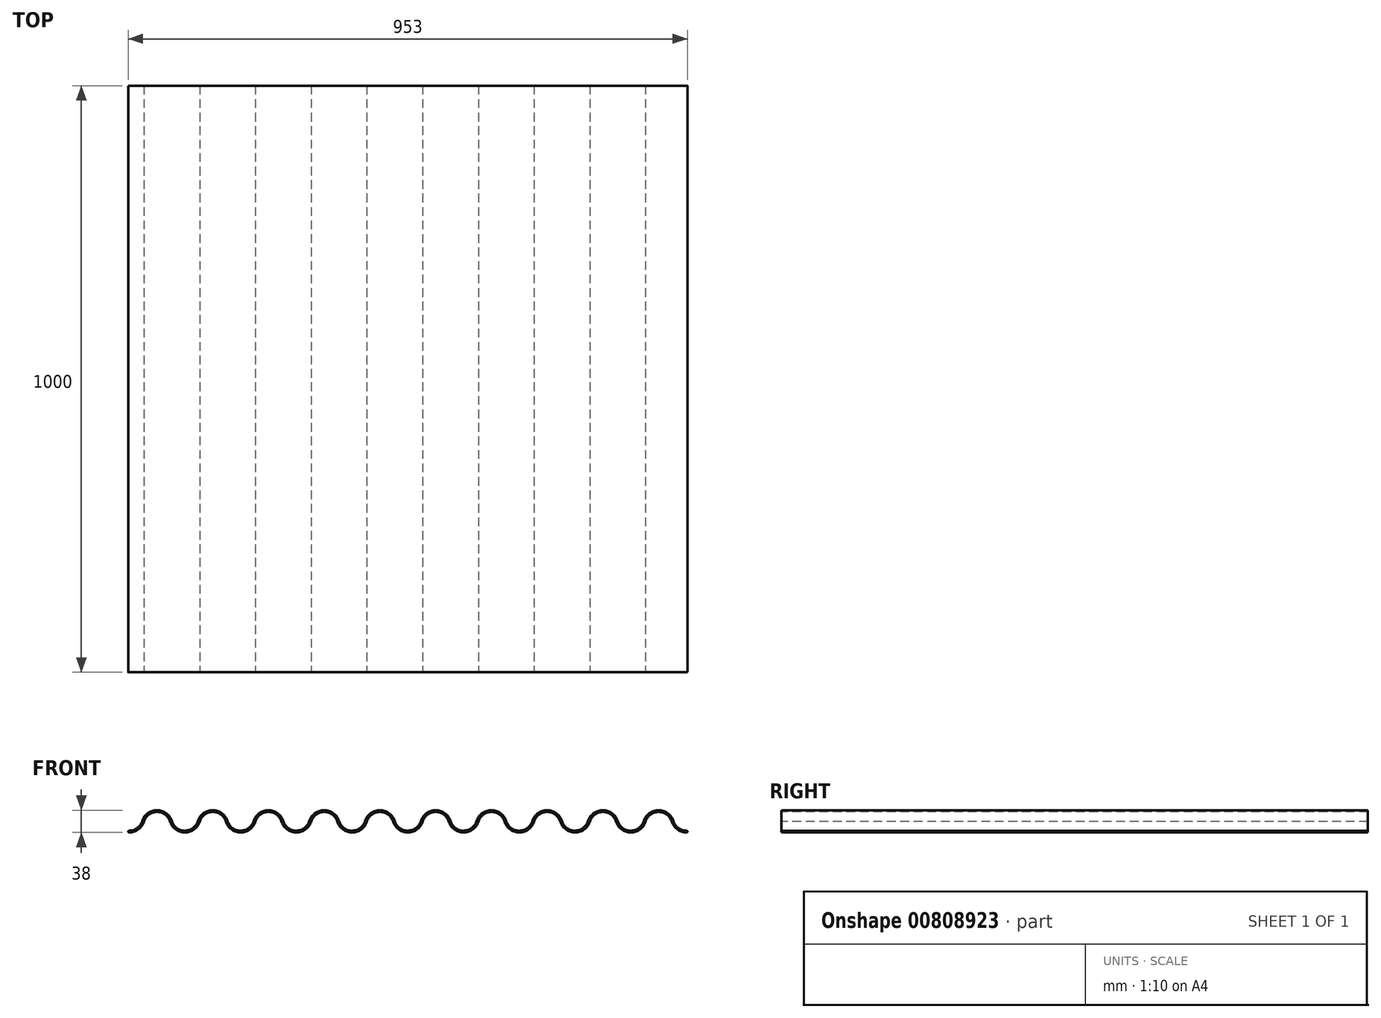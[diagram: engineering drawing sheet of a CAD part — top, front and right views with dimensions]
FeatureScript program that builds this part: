
annotation { "Feature Type Name" : "Feature", "Feature Type Description" : "" }
export const myFeature = defineFeature(function(context is Context, id is Id, definition is map)
    precondition{}
    {
        {
            var Q0;
            Q0=qCreatedBy(makeId("Front.planeOp"),FACE);
            var sketch = newSketch(context, id + "F0", { "sketchPlane" : qUnion([Q0])});
            skPoint(sketch, "E0.middle", {"position": v(0, 0) * mm});
            skArc(sketch, "E1", {"start": v(-47.5, -17.5) * mm, "mid": v(-32.61, -12.55) * mm, "end": v(-23.65, 0.32) * mm});
            skArc(sketch, "E2", {"start": v(0, 17.5) * mm, "mid": v(-14.62, 12.75) * mm, "end": v(-23.65, 0.32) * mm});
            skArc(sketch, "E3", {"start": v(23.75, 0) * mm, "mid": v(14.76, 12.66) * mm, "end": v(0, 17.5) * mm});
            skArc(sketch, "E4", {"start": v(23.75, 0) * mm, "mid": v(32.75, -12.65) * mm, "end": v(47.5, -17.5) * mm});
            skArc(sketch, "E5.0.startCap", {"start": v(-47.5, -19) * mm, "mid": v(-49, -17.5) * mm, "end": v(-47.5, -16) * mm});
            skArc(sketch, "E5.0.endCap", {"start": v(-25.1, 0.75) * mm, "mid": v(-23.23, 1.76) * mm, "end": v(-22.21, -0.1) * mm});
            skArc(sketch, "E5.0.left", {"start": v(-47.5, -16) * mm, "mid": v(-33.51, -11.35) * mm, "end": v(-25.1, 0.75) * mm});
            skArc(sketch, "E5.0.right", {"start": v(-47.5, -19) * mm, "mid": v(-31.72, -13.75) * mm, "end": v(-22.21, -0.1) * mm});
            skArc(sketch, "E5.1.startCap", {"start": v(0, 19) * mm, "mid": v(1.5, 17.5) * mm, "end": v(0, 16) * mm});
            skArc(sketch, "E5.1.endCap", {"start": v(-22.23, -0.14) * mm, "mid": v(-24.12, -1.1) * mm, "end": v(-25.08, 0.79) * mm});
            skArc(sketch, "E5.1.left", {"start": v(0, 16) * mm, "mid": v(-13.73, 11.54) * mm, "end": v(-22.23, -0.14) * mm});
            skArc(sketch, "E5.1.right", {"start": v(0, 19) * mm, "mid": v(-15.5, 13.97) * mm, "end": v(-25.08, 0.79) * mm});
            skArc(sketch, "E5.2.startCap", {"start": v(25.18, 0.44) * mm, "mid": v(24.2, -1.43) * mm, "end": v(22.32, -0.44) * mm});
            skArc(sketch, "E5.2.endCap", {"start": v(0, 16) * mm, "mid": v(-1.5, 17.5) * mm, "end": v(0, 19) * mm});
            skArc(sketch, "E5.2.left", {"start": v(22.32, -0.44) * mm, "mid": v(13.87, 11.46) * mm, "end": v(0, 16) * mm});
            skArc(sketch, "E5.2.right", {"start": v(25.18, 0.44) * mm, "mid": v(15.65, 13.87) * mm, "end": v(0, 19) * mm});
            skArc(sketch, "E5.3.startCap", {"start": v(22.32, -0.44) * mm, "mid": v(23.3, 1.43) * mm, "end": v(25.18, 0.44) * mm});
            skArc(sketch, "E5.3.endCap", {"start": v(47.5, -16) * mm, "mid": v(49, -17.5) * mm, "end": v(47.5, -19) * mm});
            skArc(sketch, "E5.3.left", {"start": v(25.18, 0.44) * mm, "mid": v(33.64, -11.44) * mm, "end": v(47.5, -16) * mm});
            skArc(sketch, "E5.3.right", {"start": v(22.32, -0.44) * mm, "mid": v(31.86, -13.86) * mm, "end": v(47.5, -19) * mm});
            skArc(sketch, "E6.1.0.0", {"start": v(47.5, -19) * mm, "mid": v(63.28, -13.75) * mm, "end": v(72.79, -0.1) * mm});
            skArc(sketch, "E6.1.0.1", {"start": v(95, 19) * mm, "mid": v(79.5, 13.97) * mm, "end": v(69.92, 0.79) * mm});
            skArc(sketch, "E6.1.0.2", {"start": v(118.75, 0) * mm, "mid": v(109.76, 12.66) * mm, "end": v(95, 17.5) * mm});
            skArc(sketch, "E6.1.0.3", {"start": v(72.77, -0.14) * mm, "mid": v(70.88, -1.1) * mm, "end": v(69.92, 0.79) * mm});
            skArc(sketch, "E6.1.0.4", {"start": v(47.5, -17.5) * mm, "mid": v(62.39, -12.55) * mm, "end": v(71.35, 0.32) * mm});
            skArc(sketch, "E6.1.0.5", {"start": v(118.75, 0) * mm, "mid": v(127.75, -12.65) * mm, "end": v(142.5, -17.5) * mm});
            skArc(sketch, "E6.1.0.6", {"start": v(95, 17.5) * mm, "mid": v(80.38, 12.75) * mm, "end": v(71.35, 0.32) * mm});
            skPoint(sketch, "E6.1.0.7", {"position": v(95, 0) * mm});
            skArc(sketch, "E6.1.0.8", {"start": v(95, 16) * mm, "mid": v(81.27, 11.54) * mm, "end": v(72.77, -0.14) * mm});
            skArc(sketch, "E6.1.0.9", {"start": v(117.32, -0.44) * mm, "mid": v(108.87, 11.46) * mm, "end": v(95, 16) * mm});
            skArc(sketch, "E6.1.0.10", {"start": v(120.18, 0.44) * mm, "mid": v(128.64, -11.44) * mm, "end": v(142.5, -16) * mm});
            skArc(sketch, "E6.1.0.11", {"start": v(95, 19) * mm, "mid": v(96.5, 17.5) * mm, "end": v(95, 16) * mm});
            skArc(sketch, "E6.1.0.12", {"start": v(47.5, -16) * mm, "mid": v(61.49, -11.35) * mm, "end": v(69.9, 0.75) * mm});
            skArc(sketch, "E6.1.0.13", {"start": v(117.32, -0.44) * mm, "mid": v(126.86, -13.86) * mm, "end": v(142.5, -19) * mm});
            skArc(sketch, "E6.1.0.14", {"start": v(120.18, 0.44) * mm, "mid": v(119.2, -1.43) * mm, "end": v(117.32, -0.44) * mm});
            skArc(sketch, "E6.1.0.15", {"start": v(47.5, -19) * mm, "mid": v(46, -17.5) * mm, "end": v(47.5, -16) * mm});
            skArc(sketch, "E6.1.0.16", {"start": v(69.9, 0.75) * mm, "mid": v(71.77, 1.76) * mm, "end": v(72.79, -0.1) * mm});
            skArc(sketch, "E6.1.0.17", {"start": v(142.5, -16) * mm, "mid": v(144, -17.5) * mm, "end": v(142.5, -19) * mm});
            skArc(sketch, "E6.1.0.18", {"start": v(120.18, 0.44) * mm, "mid": v(110.65, 13.87) * mm, "end": v(95, 19) * mm});
            skArc(sketch, "E6.1.0.19", {"start": v(117.32, -0.44) * mm, "mid": v(118.3, 1.43) * mm, "end": v(120.18, 0.44) * mm});
            skArc(sketch, "E6.1.0.20", {"start": v(95, 16) * mm, "mid": v(93.5, 17.5) * mm, "end": v(95, 19) * mm});
            skArc(sketch, "E6.2.0.0", {"start": v(142.5, -19) * mm, "mid": v(158.28, -13.75) * mm, "end": v(167.79, -0.1) * mm});
            skArc(sketch, "E6.2.0.1", {"start": v(190, 19) * mm, "mid": v(174.5, 13.97) * mm, "end": v(164.92, 0.79) * mm});
            skArc(sketch, "E6.2.0.2", {"start": v(213.75, 0) * mm, "mid": v(204.76, 12.66) * mm, "end": v(190, 17.5) * mm});
            skArc(sketch, "E6.2.0.3", {"start": v(167.77, -0.14) * mm, "mid": v(165.88, -1.1) * mm, "end": v(164.92, 0.79) * mm});
            skArc(sketch, "E6.2.0.4", {"start": v(142.5, -17.5) * mm, "mid": v(157.39, -12.55) * mm, "end": v(166.35, 0.32) * mm});
            skArc(sketch, "E6.2.0.5", {"start": v(213.75, 0) * mm, "mid": v(222.75, -12.65) * mm, "end": v(237.5, -17.5) * mm});
            skArc(sketch, "E6.2.0.6", {"start": v(190, 17.5) * mm, "mid": v(175.38, 12.75) * mm, "end": v(166.35, 0.32) * mm});
            skPoint(sketch, "E6.2.0.7", {"position": v(190, 0) * mm});
            skArc(sketch, "E6.2.0.8", {"start": v(190, 16) * mm, "mid": v(176.27, 11.54) * mm, "end": v(167.77, -0.14) * mm});
            skArc(sketch, "E6.2.0.9", {"start": v(212.32, -0.44) * mm, "mid": v(203.87, 11.46) * mm, "end": v(190, 16) * mm});
            skArc(sketch, "E6.2.0.10", {"start": v(215.18, 0.44) * mm, "mid": v(223.64, -11.44) * mm, "end": v(237.5, -16) * mm});
            skArc(sketch, "E6.2.0.11", {"start": v(190, 19) * mm, "mid": v(191.5, 17.5) * mm, "end": v(190, 16) * mm});
            skArc(sketch, "E6.2.0.12", {"start": v(142.5, -16) * mm, "mid": v(156.49, -11.35) * mm, "end": v(164.9, 0.75) * mm});
            skArc(sketch, "E6.2.0.13", {"start": v(212.32, -0.44) * mm, "mid": v(221.86, -13.86) * mm, "end": v(237.5, -19) * mm});
            skArc(sketch, "E6.2.0.14", {"start": v(215.18, 0.44) * mm, "mid": v(214.2, -1.43) * mm, "end": v(212.32, -0.44) * mm});
            skArc(sketch, "E6.2.0.15", {"start": v(142.5, -19) * mm, "mid": v(141, -17.5) * mm, "end": v(142.5, -16) * mm});
            skArc(sketch, "E6.2.0.16", {"start": v(164.9, 0.75) * mm, "mid": v(166.77, 1.76) * mm, "end": v(167.79, -0.1) * mm});
            skArc(sketch, "E6.2.0.17", {"start": v(237.5, -16) * mm, "mid": v(239, -17.5) * mm, "end": v(237.5, -19) * mm});
            skArc(sketch, "E6.2.0.18", {"start": v(215.18, 0.44) * mm, "mid": v(205.65, 13.87) * mm, "end": v(190, 19) * mm});
            skArc(sketch, "E6.2.0.19", {"start": v(212.32, -0.44) * mm, "mid": v(213.3, 1.43) * mm, "end": v(215.18, 0.44) * mm});
            skArc(sketch, "E6.2.0.20", {"start": v(190, 16) * mm, "mid": v(188.5, 17.5) * mm, "end": v(190, 19) * mm});
            skArc(sketch, "E6.3.0.0", {"start": v(237.5, -19) * mm, "mid": v(253.28, -13.75) * mm, "end": v(262.79, -0.1) * mm});
            skArc(sketch, "E6.3.0.1", {"start": v(285, 19) * mm, "mid": v(269.5, 13.97) * mm, "end": v(259.92, 0.79) * mm});
            skArc(sketch, "E6.3.0.2", {"start": v(308.75, 0) * mm, "mid": v(299.76, 12.66) * mm, "end": v(285, 17.5) * mm});
            skArc(sketch, "E6.3.0.3", {"start": v(262.77, -0.14) * mm, "mid": v(260.88, -1.1) * mm, "end": v(259.92, 0.79) * mm});
            skArc(sketch, "E6.3.0.4", {"start": v(237.5, -17.5) * mm, "mid": v(252.39, -12.55) * mm, "end": v(261.35, 0.32) * mm});
            skArc(sketch, "E6.3.0.5", {"start": v(308.75, 0) * mm, "mid": v(317.75, -12.65) * mm, "end": v(332.5, -17.5) * mm});
            skArc(sketch, "E6.3.0.6", {"start": v(285, 17.5) * mm, "mid": v(270.38, 12.75) * mm, "end": v(261.35, 0.32) * mm});
            skPoint(sketch, "E6.3.0.7", {"position": v(285, 0) * mm});
            skArc(sketch, "E6.3.0.8", {"start": v(285, 16) * mm, "mid": v(271.27, 11.54) * mm, "end": v(262.77, -0.14) * mm});
            skArc(sketch, "E6.3.0.9", {"start": v(307.32, -0.44) * mm, "mid": v(298.87, 11.46) * mm, "end": v(285, 16) * mm});
            skArc(sketch, "E6.3.0.10", {"start": v(310.18, 0.44) * mm, "mid": v(318.64, -11.44) * mm, "end": v(332.5, -16) * mm});
            skArc(sketch, "E6.3.0.11", {"start": v(285, 19) * mm, "mid": v(286.5, 17.5) * mm, "end": v(285, 16) * mm});
            skArc(sketch, "E6.3.0.12", {"start": v(237.5, -16) * mm, "mid": v(251.49, -11.35) * mm, "end": v(259.9, 0.75) * mm});
            skArc(sketch, "E6.3.0.13", {"start": v(307.32, -0.44) * mm, "mid": v(316.86, -13.86) * mm, "end": v(332.5, -19) * mm});
            skArc(sketch, "E6.3.0.14", {"start": v(310.18, 0.44) * mm, "mid": v(309.2, -1.43) * mm, "end": v(307.32, -0.44) * mm});
            skArc(sketch, "E6.3.0.15", {"start": v(237.5, -19) * mm, "mid": v(236, -17.5) * mm, "end": v(237.5, -16) * mm});
            skArc(sketch, "E6.3.0.16", {"start": v(259.9, 0.75) * mm, "mid": v(261.77, 1.76) * mm, "end": v(262.79, -0.1) * mm});
            skArc(sketch, "E6.3.0.17", {"start": v(332.5, -16) * mm, "mid": v(334, -17.5) * mm, "end": v(332.5, -19) * mm});
            skArc(sketch, "E6.3.0.18", {"start": v(310.18, 0.44) * mm, "mid": v(300.65, 13.87) * mm, "end": v(285, 19) * mm});
            skArc(sketch, "E6.3.0.19", {"start": v(307.32, -0.44) * mm, "mid": v(308.3, 1.43) * mm, "end": v(310.18, 0.44) * mm});
            skArc(sketch, "E6.3.0.20", {"start": v(285, 16) * mm, "mid": v(283.5, 17.5) * mm, "end": v(285, 19) * mm});
            skArc(sketch, "E6.4.0.0", {"start": v(332.5, -19) * mm, "mid": v(348.28, -13.75) * mm, "end": v(357.79, -0.1) * mm});
            skArc(sketch, "E6.4.0.1", {"start": v(380, 19) * mm, "mid": v(364.5, 13.97) * mm, "end": v(354.92, 0.79) * mm});
            skArc(sketch, "E6.4.0.2", {"start": v(403.75, 0) * mm, "mid": v(394.76, 12.66) * mm, "end": v(380, 17.5) * mm});
            skArc(sketch, "E6.4.0.3", {"start": v(357.77, -0.14) * mm, "mid": v(355.88, -1.1) * mm, "end": v(354.92, 0.79) * mm});
            skArc(sketch, "E6.4.0.4", {"start": v(332.5, -17.5) * mm, "mid": v(347.39, -12.55) * mm, "end": v(356.35, 0.32) * mm});
            skArc(sketch, "E6.4.0.5", {"start": v(403.75, 0) * mm, "mid": v(412.75, -12.65) * mm, "end": v(427.5, -17.5) * mm});
            skArc(sketch, "E6.4.0.6", {"start": v(380, 17.5) * mm, "mid": v(365.38, 12.75) * mm, "end": v(356.35, 0.32) * mm});
            skPoint(sketch, "E6.4.0.7", {"position": v(380, 0) * mm});
            skArc(sketch, "E6.4.0.8", {"start": v(380, 16) * mm, "mid": v(366.27, 11.54) * mm, "end": v(357.77, -0.14) * mm});
            skArc(sketch, "E6.4.0.9", {"start": v(402.32, -0.44) * mm, "mid": v(393.87, 11.46) * mm, "end": v(380, 16) * mm});
            skArc(sketch, "E6.4.0.10", {"start": v(405.18, 0.44) * mm, "mid": v(413.64, -11.44) * mm, "end": v(427.5, -16) * mm});
            skArc(sketch, "E6.4.0.11", {"start": v(380, 19) * mm, "mid": v(381.5, 17.5) * mm, "end": v(380, 16) * mm});
            skArc(sketch, "E6.4.0.12", {"start": v(332.5, -16) * mm, "mid": v(346.49, -11.35) * mm, "end": v(354.9, 0.75) * mm});
            skArc(sketch, "E6.4.0.13", {"start": v(402.32, -0.44) * mm, "mid": v(411.86, -13.86) * mm, "end": v(427.5, -19) * mm});
            skArc(sketch, "E6.4.0.14", {"start": v(405.18, 0.44) * mm, "mid": v(404.2, -1.43) * mm, "end": v(402.32, -0.44) * mm});
            skArc(sketch, "E6.4.0.15", {"start": v(332.5, -19) * mm, "mid": v(331, -17.5) * mm, "end": v(332.5, -16) * mm});
            skArc(sketch, "E6.4.0.16", {"start": v(354.9, 0.75) * mm, "mid": v(356.77, 1.76) * mm, "end": v(357.79, -0.1) * mm});
            skArc(sketch, "E6.4.0.17", {"start": v(427.5, -16) * mm, "mid": v(429, -17.5) * mm, "end": v(427.5, -19) * mm});
            skArc(sketch, "E6.4.0.18", {"start": v(405.18, 0.44) * mm, "mid": v(395.65, 13.87) * mm, "end": v(380, 19) * mm});
            skArc(sketch, "E6.4.0.19", {"start": v(402.32, -0.44) * mm, "mid": v(403.3, 1.43) * mm, "end": v(405.18, 0.44) * mm});
            skArc(sketch, "E6.4.0.20", {"start": v(380, 16) * mm, "mid": v(378.5, 17.5) * mm, "end": v(380, 19) * mm});
            skArc(sketch, "E6.5.0.0", {"start": v(427.5, -19) * mm, "mid": v(443.28, -13.75) * mm, "end": v(452.79, -0.1) * mm});
            skArc(sketch, "E6.5.0.1", {"start": v(475, 19) * mm, "mid": v(459.5, 13.97) * mm, "end": v(449.92, 0.79) * mm});
            skArc(sketch, "E6.5.0.2", {"start": v(498.75, 0) * mm, "mid": v(489.76, 12.66) * mm, "end": v(475, 17.5) * mm});
            skArc(sketch, "E6.5.0.3", {"start": v(452.77, -0.14) * mm, "mid": v(450.88, -1.1) * mm, "end": v(449.92, 0.79) * mm});
            skArc(sketch, "E6.5.0.4", {"start": v(427.5, -17.5) * mm, "mid": v(442.39, -12.55) * mm, "end": v(451.35, 0.32) * mm});
            skArc(sketch, "E6.5.0.5", {"start": v(498.75, 0) * mm, "mid": v(507.75, -12.65) * mm, "end": v(522.5, -17.5) * mm});
            skArc(sketch, "E6.5.0.6", {"start": v(475, 17.5) * mm, "mid": v(460.38, 12.75) * mm, "end": v(451.35, 0.32) * mm});
            skPoint(sketch, "E6.5.0.7", {"position": v(475, 0) * mm});
            skArc(sketch, "E6.5.0.8", {"start": v(475, 16) * mm, "mid": v(461.27, 11.54) * mm, "end": v(452.77, -0.14) * mm});
            skArc(sketch, "E6.5.0.9", {"start": v(497.32, -0.44) * mm, "mid": v(488.87, 11.46) * mm, "end": v(475, 16) * mm});
            skArc(sketch, "E6.5.0.10", {"start": v(500.18, 0.44) * mm, "mid": v(508.64, -11.44) * mm, "end": v(522.5, -16) * mm});
            skArc(sketch, "E6.5.0.11", {"start": v(475, 19) * mm, "mid": v(476.5, 17.5) * mm, "end": v(475, 16) * mm});
            skArc(sketch, "E6.5.0.12", {"start": v(427.5, -16) * mm, "mid": v(441.49, -11.35) * mm, "end": v(449.9, 0.75) * mm});
            skArc(sketch, "E6.5.0.13", {"start": v(497.32, -0.44) * mm, "mid": v(506.86, -13.86) * mm, "end": v(522.5, -19) * mm});
            skArc(sketch, "E6.5.0.14", {"start": v(500.18, 0.44) * mm, "mid": v(499.2, -1.43) * mm, "end": v(497.32, -0.44) * mm});
            skArc(sketch, "E6.5.0.15", {"start": v(427.5, -19) * mm, "mid": v(426, -17.5) * mm, "end": v(427.5, -16) * mm});
            skArc(sketch, "E6.5.0.16", {"start": v(449.9, 0.75) * mm, "mid": v(451.77, 1.76) * mm, "end": v(452.79, -0.1) * mm});
            skArc(sketch, "E6.5.0.17", {"start": v(522.5, -16) * mm, "mid": v(524, -17.5) * mm, "end": v(522.5, -19) * mm});
            skArc(sketch, "E6.5.0.18", {"start": v(500.18, 0.44) * mm, "mid": v(490.65, 13.87) * mm, "end": v(475, 19) * mm});
            skArc(sketch, "E6.5.0.19", {"start": v(497.32, -0.44) * mm, "mid": v(498.3, 1.43) * mm, "end": v(500.18, 0.44) * mm});
            skArc(sketch, "E6.5.0.20", {"start": v(475, 16) * mm, "mid": v(473.5, 17.5) * mm, "end": v(475, 19) * mm});
            skArc(sketch, "E6.6.0.0", {"start": v(522.5, -19) * mm, "mid": v(538.28, -13.75) * mm, "end": v(547.79, -0.1) * mm});
            skArc(sketch, "E6.6.0.1", {"start": v(570, 19) * mm, "mid": v(554.5, 13.97) * mm, "end": v(544.92, 0.79) * mm});
            skArc(sketch, "E6.6.0.2", {"start": v(593.75, 0) * mm, "mid": v(584.76, 12.66) * mm, "end": v(570, 17.5) * mm});
            skArc(sketch, "E6.6.0.3", {"start": v(547.77, -0.14) * mm, "mid": v(545.88, -1.1) * mm, "end": v(544.92, 0.79) * mm});
            skArc(sketch, "E6.6.0.4", {"start": v(522.5, -17.5) * mm, "mid": v(537.39, -12.55) * mm, "end": v(546.35, 0.32) * mm});
            skArc(sketch, "E6.6.0.5", {"start": v(593.75, 0) * mm, "mid": v(602.75, -12.65) * mm, "end": v(617.5, -17.5) * mm});
            skArc(sketch, "E6.6.0.6", {"start": v(570, 17.5) * mm, "mid": v(555.38, 12.75) * mm, "end": v(546.35, 0.32) * mm});
            skPoint(sketch, "E6.6.0.7", {"position": v(570, 0) * mm});
            skArc(sketch, "E6.6.0.8", {"start": v(570, 16) * mm, "mid": v(556.27, 11.54) * mm, "end": v(547.77, -0.14) * mm});
            skArc(sketch, "E6.6.0.9", {"start": v(592.32, -0.44) * mm, "mid": v(583.87, 11.46) * mm, "end": v(570, 16) * mm});
            skArc(sketch, "E6.6.0.10", {"start": v(595.18, 0.44) * mm, "mid": v(603.64, -11.44) * mm, "end": v(617.5, -16) * mm});
            skArc(sketch, "E6.6.0.11", {"start": v(570, 19) * mm, "mid": v(571.5, 17.5) * mm, "end": v(570, 16) * mm});
            skArc(sketch, "E6.6.0.12", {"start": v(522.5, -16) * mm, "mid": v(536.49, -11.35) * mm, "end": v(544.9, 0.75) * mm});
            skArc(sketch, "E6.6.0.13", {"start": v(592.32, -0.44) * mm, "mid": v(601.86, -13.86) * mm, "end": v(617.5, -19) * mm});
            skArc(sketch, "E6.6.0.14", {"start": v(595.18, 0.44) * mm, "mid": v(594.2, -1.43) * mm, "end": v(592.32, -0.44) * mm});
            skArc(sketch, "E6.6.0.15", {"start": v(522.5, -19) * mm, "mid": v(521, -17.5) * mm, "end": v(522.5, -16) * mm});
            skArc(sketch, "E6.6.0.16", {"start": v(544.9, 0.75) * mm, "mid": v(546.77, 1.76) * mm, "end": v(547.79, -0.1) * mm});
            skArc(sketch, "E6.6.0.17", {"start": v(617.5, -16) * mm, "mid": v(619, -17.5) * mm, "end": v(617.5, -19) * mm});
            skArc(sketch, "E6.6.0.18", {"start": v(595.18, 0.44) * mm, "mid": v(585.65, 13.87) * mm, "end": v(570, 19) * mm});
            skArc(sketch, "E6.6.0.19", {"start": v(592.32, -0.44) * mm, "mid": v(593.3, 1.43) * mm, "end": v(595.18, 0.44) * mm});
            skArc(sketch, "E6.6.0.20", {"start": v(570, 16) * mm, "mid": v(568.5, 17.5) * mm, "end": v(570, 19) * mm});
            skArc(sketch, "E6.7.0.0", {"start": v(617.5, -19) * mm, "mid": v(633.28, -13.75) * mm, "end": v(642.79, -0.1) * mm});
            skArc(sketch, "E6.7.0.1", {"start": v(665, 19) * mm, "mid": v(649.5, 13.97) * mm, "end": v(639.92, 0.79) * mm});
            skArc(sketch, "E6.7.0.2", {"start": v(688.75, 0) * mm, "mid": v(679.76, 12.66) * mm, "end": v(665, 17.5) * mm});
            skArc(sketch, "E6.7.0.3", {"start": v(642.77, -0.14) * mm, "mid": v(640.88, -1.1) * mm, "end": v(639.92, 0.79) * mm});
            skArc(sketch, "E6.7.0.4", {"start": v(617.5, -17.5) * mm, "mid": v(632.39, -12.55) * mm, "end": v(641.35, 0.32) * mm});
            skArc(sketch, "E6.7.0.5", {"start": v(688.75, 0) * mm, "mid": v(697.75, -12.65) * mm, "end": v(712.5, -17.5) * mm});
            skArc(sketch, "E6.7.0.6", {"start": v(665, 17.5) * mm, "mid": v(650.38, 12.75) * mm, "end": v(641.35, 0.32) * mm});
            skPoint(sketch, "E6.7.0.7", {"position": v(665, 0) * mm});
            skArc(sketch, "E6.7.0.8", {"start": v(665, 16) * mm, "mid": v(651.27, 11.54) * mm, "end": v(642.77, -0.14) * mm});
            skArc(sketch, "E6.7.0.9", {"start": v(687.32, -0.44) * mm, "mid": v(678.87, 11.46) * mm, "end": v(665, 16) * mm});
            skArc(sketch, "E6.7.0.10", {"start": v(690.18, 0.44) * mm, "mid": v(698.64, -11.44) * mm, "end": v(712.5, -16) * mm});
            skArc(sketch, "E6.7.0.11", {"start": v(665, 19) * mm, "mid": v(666.5, 17.5) * mm, "end": v(665, 16) * mm});
            skArc(sketch, "E6.7.0.12", {"start": v(617.5, -16) * mm, "mid": v(631.49, -11.35) * mm, "end": v(639.9, 0.75) * mm});
            skArc(sketch, "E6.7.0.13", {"start": v(687.32, -0.44) * mm, "mid": v(696.86, -13.86) * mm, "end": v(712.5, -19) * mm});
            skArc(sketch, "E6.7.0.14", {"start": v(690.18, 0.44) * mm, "mid": v(689.2, -1.43) * mm, "end": v(687.32, -0.44) * mm});
            skArc(sketch, "E6.7.0.15", {"start": v(617.5, -19) * mm, "mid": v(616, -17.5) * mm, "end": v(617.5, -16) * mm});
            skArc(sketch, "E6.7.0.16", {"start": v(639.9, 0.75) * mm, "mid": v(641.77, 1.76) * mm, "end": v(642.79, -0.1) * mm});
            skArc(sketch, "E6.7.0.17", {"start": v(712.5, -16) * mm, "mid": v(714, -17.5) * mm, "end": v(712.5, -19) * mm});
            skArc(sketch, "E6.7.0.18", {"start": v(690.18, 0.44) * mm, "mid": v(680.65, 13.87) * mm, "end": v(665, 19) * mm});
            skArc(sketch, "E6.7.0.19", {"start": v(687.32, -0.44) * mm, "mid": v(688.3, 1.43) * mm, "end": v(690.18, 0.44) * mm});
            skArc(sketch, "E6.7.0.20", {"start": v(665, 16) * mm, "mid": v(663.5, 17.5) * mm, "end": v(665, 19) * mm});
            skArc(sketch, "E6.8.0.0", {"start": v(712.5, -19) * mm, "mid": v(728.28, -13.75) * mm, "end": v(737.79, -0.1) * mm});
            skArc(sketch, "E6.8.0.1", {"start": v(760, 19) * mm, "mid": v(744.5, 13.97) * mm, "end": v(734.92, 0.79) * mm});
            skArc(sketch, "E6.8.0.2", {"start": v(783.75, 0) * mm, "mid": v(774.76, 12.66) * mm, "end": v(760, 17.5) * mm});
            skArc(sketch, "E6.8.0.3", {"start": v(737.77, -0.14) * mm, "mid": v(735.88, -1.1) * mm, "end": v(734.92, 0.79) * mm});
            skArc(sketch, "E6.8.0.4", {"start": v(712.5, -17.5) * mm, "mid": v(727.39, -12.55) * mm, "end": v(736.35, 0.32) * mm});
            skArc(sketch, "E6.8.0.5", {"start": v(783.75, 0) * mm, "mid": v(792.75, -12.65) * mm, "end": v(807.5, -17.5) * mm});
            skArc(sketch, "E6.8.0.6", {"start": v(760, 17.5) * mm, "mid": v(745.38, 12.75) * mm, "end": v(736.35, 0.32) * mm});
            skPoint(sketch, "E6.8.0.7", {"position": v(760, 0) * mm});
            skArc(sketch, "E6.8.0.8", {"start": v(760, 16) * mm, "mid": v(746.27, 11.54) * mm, "end": v(737.77, -0.14) * mm});
            skArc(sketch, "E6.8.0.9", {"start": v(782.32, -0.44) * mm, "mid": v(773.87, 11.46) * mm, "end": v(760, 16) * mm});
            skArc(sketch, "E6.8.0.10", {"start": v(785.18, 0.44) * mm, "mid": v(793.64, -11.44) * mm, "end": v(807.5, -16) * mm});
            skArc(sketch, "E6.8.0.11", {"start": v(760, 19) * mm, "mid": v(761.5, 17.5) * mm, "end": v(760, 16) * mm});
            skArc(sketch, "E6.8.0.12", {"start": v(712.5, -16) * mm, "mid": v(726.49, -11.35) * mm, "end": v(734.9, 0.75) * mm});
            skArc(sketch, "E6.8.0.13", {"start": v(782.32, -0.44) * mm, "mid": v(791.86, -13.86) * mm, "end": v(807.5, -19) * mm});
            skArc(sketch, "E6.8.0.14", {"start": v(785.18, 0.44) * mm, "mid": v(784.2, -1.43) * mm, "end": v(782.32, -0.44) * mm});
            skArc(sketch, "E6.8.0.15", {"start": v(712.5, -19) * mm, "mid": v(711, -17.5) * mm, "end": v(712.5, -16) * mm});
            skArc(sketch, "E6.8.0.16", {"start": v(734.9, 0.75) * mm, "mid": v(736.77, 1.76) * mm, "end": v(737.79, -0.1) * mm});
            skArc(sketch, "E6.8.0.17", {"start": v(807.5, -16) * mm, "mid": v(809, -17.5) * mm, "end": v(807.5, -19) * mm});
            skArc(sketch, "E6.8.0.18", {"start": v(785.18, 0.44) * mm, "mid": v(775.65, 13.87) * mm, "end": v(760, 19) * mm});
            skArc(sketch, "E6.8.0.19", {"start": v(782.32, -0.44) * mm, "mid": v(783.3, 1.43) * mm, "end": v(785.18, 0.44) * mm});
            skArc(sketch, "E6.8.0.20", {"start": v(760, 16) * mm, "mid": v(758.5, 17.5) * mm, "end": v(760, 19) * mm});
            skArc(sketch, "E6.9.0.0", {"start": v(807.5, -19) * mm, "mid": v(823.28, -13.75) * mm, "end": v(832.79, -0.1) * mm});
            skArc(sketch, "E6.9.0.1", {"start": v(855, 19) * mm, "mid": v(839.5, 13.97) * mm, "end": v(829.92, 0.79) * mm});
            skArc(sketch, "E6.9.0.2", {"start": v(878.75, 0) * mm, "mid": v(869.76, 12.66) * mm, "end": v(855, 17.5) * mm});
            skArc(sketch, "E6.9.0.3", {"start": v(832.77, -0.14) * mm, "mid": v(830.88, -1.1) * mm, "end": v(829.92, 0.79) * mm});
            skArc(sketch, "E6.9.0.4", {"start": v(807.5, -17.5) * mm, "mid": v(822.39, -12.55) * mm, "end": v(831.35, 0.32) * mm});
            skArc(sketch, "E6.9.0.5", {"start": v(878.75, 0) * mm, "mid": v(887.75, -12.65) * mm, "end": v(902.5, -17.5) * mm});
            skArc(sketch, "E6.9.0.6", {"start": v(855, 17.5) * mm, "mid": v(840.38, 12.75) * mm, "end": v(831.35, 0.32) * mm});
            skPoint(sketch, "E6.9.0.7", {"position": v(855, 0) * mm});
            skArc(sketch, "E6.9.0.8", {"start": v(855, 16) * mm, "mid": v(841.27, 11.54) * mm, "end": v(832.77, -0.14) * mm});
            skArc(sketch, "E6.9.0.9", {"start": v(877.32, -0.44) * mm, "mid": v(868.87, 11.46) * mm, "end": v(855, 16) * mm});
            skArc(sketch, "E6.9.0.10", {"start": v(880.18, 0.44) * mm, "mid": v(888.64, -11.44) * mm, "end": v(902.5, -16) * mm});
            skArc(sketch, "E6.9.0.11", {"start": v(855, 19) * mm, "mid": v(856.5, 17.5) * mm, "end": v(855, 16) * mm});
            skArc(sketch, "E6.9.0.12", {"start": v(807.5, -16) * mm, "mid": v(821.49, -11.35) * mm, "end": v(829.9, 0.75) * mm});
            skArc(sketch, "E6.9.0.13", {"start": v(877.32, -0.44) * mm, "mid": v(886.86, -13.86) * mm, "end": v(902.5, -19) * mm});
            skArc(sketch, "E6.9.0.14", {"start": v(880.18, 0.44) * mm, "mid": v(879.2, -1.43) * mm, "end": v(877.32, -0.44) * mm});
            skArc(sketch, "E6.9.0.15", {"start": v(807.5, -19) * mm, "mid": v(806, -17.5) * mm, "end": v(807.5, -16) * mm});
            skArc(sketch, "E6.9.0.16", {"start": v(829.9, 0.75) * mm, "mid": v(831.77, 1.76) * mm, "end": v(832.79, -0.1) * mm});
            skArc(sketch, "E6.9.0.17", {"start": v(902.5, -16) * mm, "mid": v(904, -17.5) * mm, "end": v(902.5, -19) * mm});
            skArc(sketch, "E6.9.0.18", {"start": v(880.18, 0.44) * mm, "mid": v(870.65, 13.87) * mm, "end": v(855, 19) * mm});
            skArc(sketch, "E6.9.0.19", {"start": v(877.32, -0.44) * mm, "mid": v(878.3, 1.43) * mm, "end": v(880.18, 0.44) * mm});
            skArc(sketch, "E6.9.0.20", {"start": v(855, 16) * mm, "mid": v(853.5, 17.5) * mm, "end": v(855, 19) * mm});
            skLineSegment(sketch, "E6.direction1", {"start": v(-47.5, -19) * mm, "end": v(47.5, -19) * mm, "construction": true});
            skSolve(sketch);
        }
        {
            var Q0;
            Q0=qSketchRegion(id+"F0",true);
            extrude(context, id + "F1", {"entities" : qUnion([Q0]), "oppositeDirection" : true, "depth" : 1000 * mm, "offsetDistance" : 25 * mm});
        }
    });
